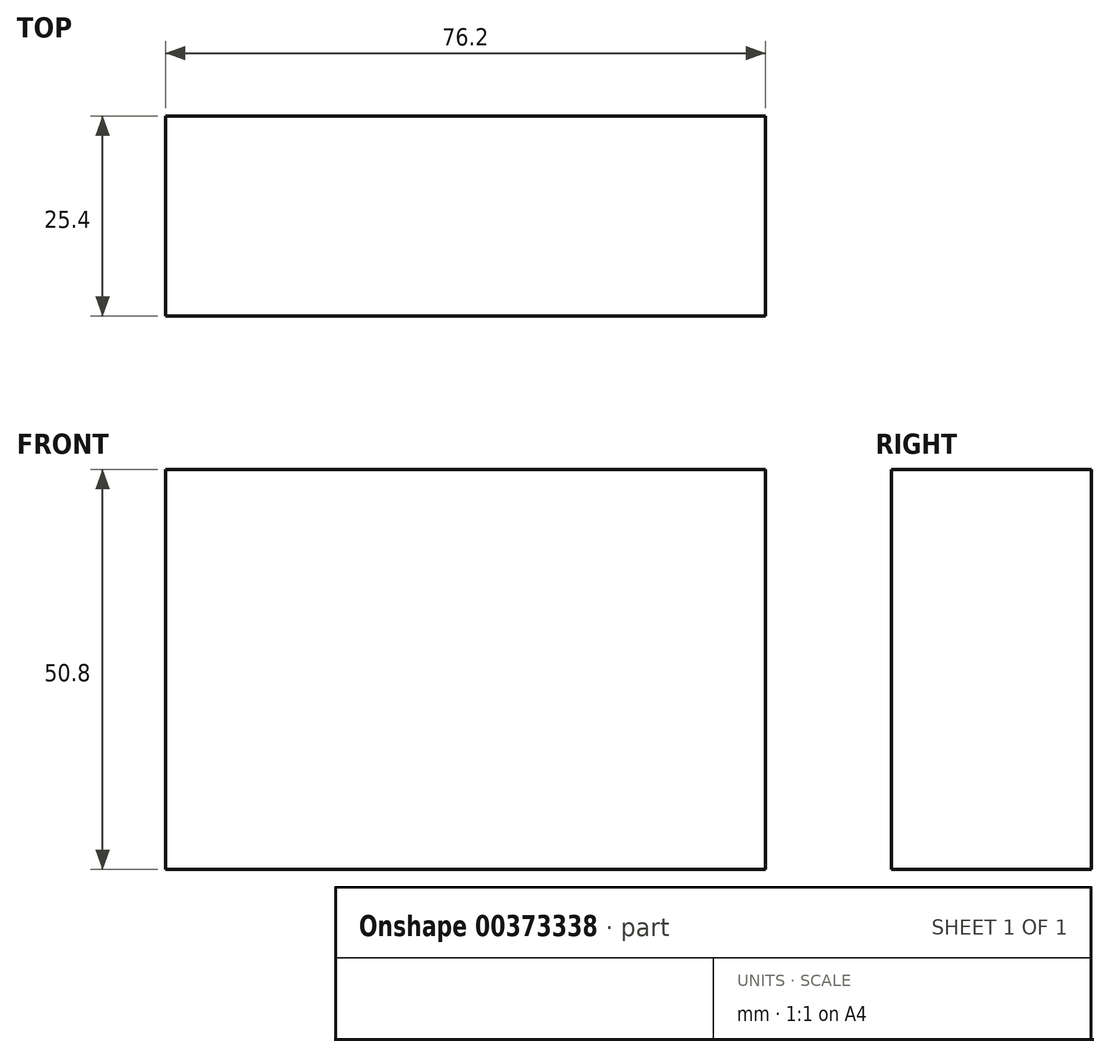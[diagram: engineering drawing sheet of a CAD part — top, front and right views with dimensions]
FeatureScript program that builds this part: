
annotation { "Feature Type Name" : "Feature", "Feature Type Description" : "" }
export const myFeature = defineFeature(function(context is Context, id is Id, definition is map)
    precondition{}
    {
        {
            var Q0;
            Q0=qCreatedBy(makeId("Front.planeOp"),FACE);
            var sketch = newSketch(context, id + "F0", { "sketchPlane" : qUnion([Q0])});
            skLineSegment(sketch, "E0", {"start": v(0, 50.8) * mm, "end": v(0, 0) * mm});
            skLineSegment(sketch, "E1", {"start": v(0, 0) * mm, "end": v(76.2, 0) * mm});
            skLineSegment(sketch, "E2", {"start": v(76.2, 0) * mm, "end": v(76.2, 50.8) * mm});
            skLineSegment(sketch, "E3", {"start": v(76.2, 50.8) * mm, "end": v(0, 50.8) * mm});
            skSolve(sketch);
        }
        {
            var Q0;
            Q0=makeQuery(id+"F0.imprint","IMPRINT",FACE,{"disambiguationData":[TD([[makeQuery(id+"F0.imprint","IMPRINT",EDGE,{"derivedFrom":sQuery(id+"F0.wireOp",EDGE,"E0")}),1.0]])]});
            extrude(context, id + "F1", {"entities" : qUnion([Q0]), "depth" : 25.4 * mm});
        }
    });
